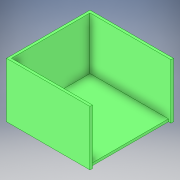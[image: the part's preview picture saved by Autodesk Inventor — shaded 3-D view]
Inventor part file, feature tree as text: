
AUTODESK INVENTOR PART (.ipt)
format: ipt  version: 2019 (Build 230136000, 136)  size: 124,928 bytes
history: native  units: mm
features: extrude x2, sketch x2, projected_geometry x1
ambient origin geometry x8: Origin, YZ Plane, XZ Plane, XY Plane, X Axis, Y Axis, Z Axis, Center Point
bodies: Solid1 (feature_tree)
feature tree (5):
  extrude  "Extrusion1"  Depth=100.0mm
  extrude  "Extrusion2"  Depth=3.18mm
  sketch  "Sketch1"  dims[d0=100.0mm d1=100.0mm]
  sketch  "Sketch2"  dims[d2=3.18mm d3=0.0mm d4=3.18mm d5=3.18mm d6=3.18mm d7=3.18mm d8=70.0mm d9=0.0mm]
  projected_geometry  "Projected Loop1"
